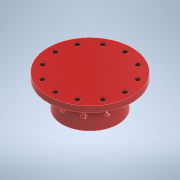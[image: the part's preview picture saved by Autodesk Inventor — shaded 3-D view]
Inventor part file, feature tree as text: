
AUTODESK INVENTOR PART (.ipt)
format: ipt  version: 2022.2 (Build 262287000, 287)  size: 233,984 bytes
history: native  units: mm
features: sketch x4, extrude x2, hole x2, plane x1, pattern_circular x1
ambient origin geometry x8: Origin, YZ Plane, XZ Plane, XY Plane, X Axis, Y Axis, Z Axis, Center Point
bodies: Body1 (feature_tree)
feature tree (10):
  extrude  "Extrusion26"  Depth=8.0mm
  hole  "Hole9"  [1 undecoded]
  extrude  "Extrusion29"  Depth=10.0mm
  plane  "Work Plane6"
  hole  "Hole10"  [1 undecoded]
  pattern_circular  "Circular Pattern1"  [2 undecoded]
  sketch  "Sketch51"  dims[d242=114.3mm d243=8.0mm]
  sketch  "Sketch58"  dims[d244=0.0mm d294=47.625mm]
  sketch  "Sketch59"  dims[d295=120.0mm d297=360.0deg]
  sketch  "Sketch60"  dims[d299=5.105mm d300=6.0mm d301=6.3754mm d302=9.525mm d303=14.3117mm d304=8.0mm d305=0.0mm d306=76.2mm d307=9.525mm d308=35.0mm d309=0.0mm d310=6.3754mm d311=6.0mm d312=6.985mm d313=5.76834mm d314=14.3117mm d315=10.0mm d316=0.0mm d317=100.0mm d318=360.0deg d64=1.0mm d65=1.0mm d66=1.0mm d67=0.15mm d68=0.25mm d69=0.375mm d70=14.3117mm d71=0.75mm d72=20.594885mm d73=0.0625mm d74=0.75mm d75=0.375mm]
note: 4 required parameter values undecoded (feature->parameter linkage not recoverable at this tier; creation-order binding heuristic only, values carry confidence <= 0.55)
